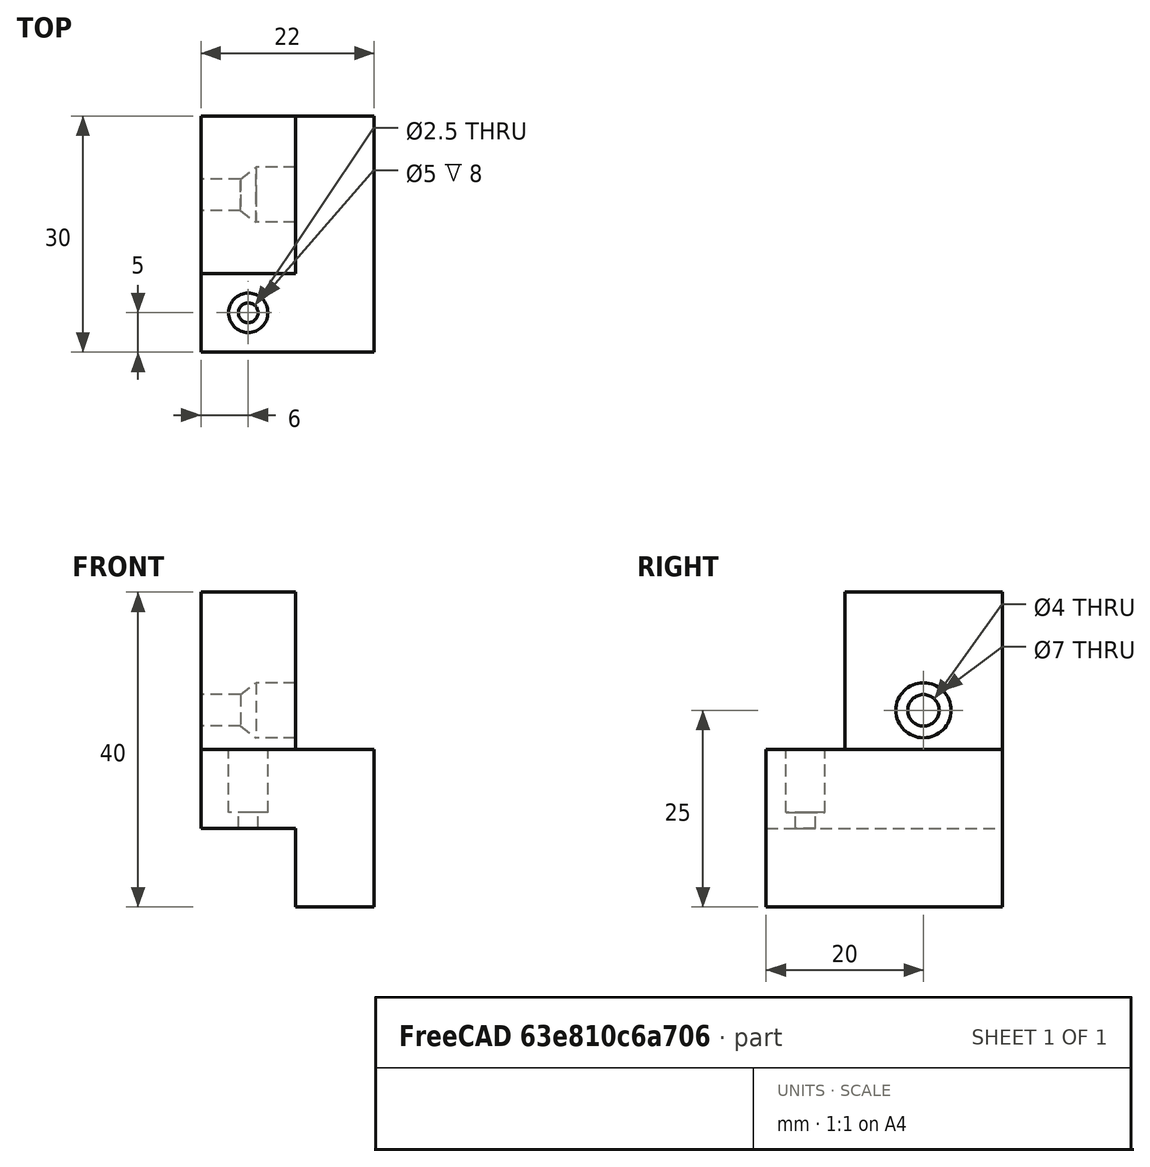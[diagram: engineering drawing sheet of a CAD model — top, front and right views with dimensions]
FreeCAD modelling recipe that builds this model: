
FCSTD DOCUMENT  (FreeCAD 0.16R6703 (Git))
Label: Anclaje Placa Superior
License: All rights reserved
LicenseURL: http://en.wikipedia.org/wiki/All_rights_reserved
objects: Part::Cylinder×4, Part::MultiFuse×4, Part::Box×3, Part::Cut×2, Part::Cone×1
note: 14 computed .brp shape members not serialized (recipe doc carries the construction recipe); baked Part::Feature solids carry a one-line shape summary decoded from their .brp

FEATURE [Part::Cylinder] Cylinder
  Angle = 360
  Height = 2
  Placement = pos=(0,-3,0) rot=(0,0,1;0rad)
  Radius = 1.25
FEATURE [Part::Cylinder] Cylinder001
  Angle = 360
  Height = 10
  Placement = pos=(0,-3,2) rot=(0,0,1;0rad)
  Radius = 2.5
FEATURE [Part::Box] Box  label="Cube"
  Height = 30
  Length = 12
  Placement = pos=(-6,-10,0) rot=(0,0,1;0rad)
  Width = 30
FEATURE [Part::Box] Box001  label="Cube001"
  Height = 20
  Length = 10
  Placement = pos=(6,-10,-10) rot=(0,0,1;0rad)
  Width = 30
FEATURE [Part::Cylinder] Cylinder002
  Angle = 360
  Height = 5
  Placement = pos=(15,-5,5) rot=(0,0,1;0rad)
  Radius = 2
FEATURE [Part::Cylinder] Cylinder003
  Angle = 360
  Height = 20
  Placement = pos=(15,-5,-17) rot=(0,0,1;0rad)
  Radius = 3.5
FEATURE [Part::Cone] Cone
  Angle = 360
  Height = 2
  Placement = pos=(15,-5,5) rot=(1,0,0;3.14159rad)
  Radius1 = 2
  Radius2 = 3.5
FEATURE [Part::MultiFuse] Fusion
  Placement = pos=(4,15,0) rot=(0,-1,0;1.5708rad)
  Shapes = -> [Cylinder002,Cylinder003,Cone]
FEATURE [Part::Box] Box002  label="Cube002"
  Height = 20
  Length = 12
  Placement = pos=(-6,-10,10) rot=(0,0,1;0rad)
  Width = 10
FEATURE [Part::MultiFuse] Fusion001
  Shapes = -> [Box,Box001]
FEATURE [Part::Cut] Cut
  Base = -> Fusion001
  Tool = -> Box002
FEATURE [Part::MultiFuse] Fusion002
  Placement = pos=(0,-2,0) rot=(0,0,1;0rad)
  Shapes = -> [Cylinder,Cylinder001]
FEATURE [Part::MultiFuse] Fusion003
  Shapes = -> [Fusion,Fusion002]
FEATURE [Part::Cut] Cut001
  Base = -> Cut
  Tool = -> Fusion003
